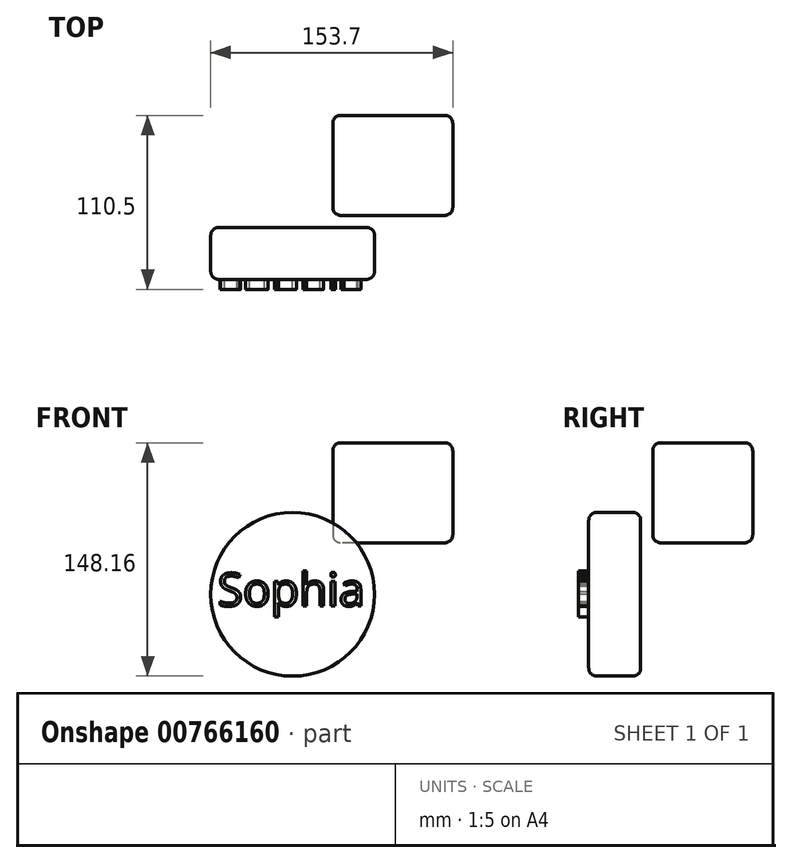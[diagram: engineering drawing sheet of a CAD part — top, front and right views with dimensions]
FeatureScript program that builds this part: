
annotation { "Feature Type Name" : "Feature", "Feature Type Description" : "" }
export const myFeature = defineFeature(function(context is Context, id is Id, definition is map)
    precondition{}
    {
        {
            var Q0;
            Q0=qCreatedBy(makeId("Front.planeOp"),FACE);
            var sketch = newSketch(context, id + "F0", { "sketchPlane" : qUnion([Q0])});
            skCircle(sketch, "E0", {"center": v(-25.5, -28.5) * mm, "radius": 52 * mm});
            skSolve(sketch);
        }
        {
            var Q0;
            Q0 = qSketchRegion(id + "F0", true);
            extrude(context, id + "F1", {"entities" : qUnion([Q0]), "depth" : 33.02 * mm, "offsetDistance" : 25.4 * mm});
        }
        {
            var Q0;
            Q0=makeQuery(id+"F1.opExtrude","SWEPT_FACE",FACE,{"disambiguationData":[OSD([sQuery(id+"F0.wireOp",EDGE,"E0")])]});
            fillet(context, id + "F2", {"entities" : qUnion([Q0]), "radius" : 5.08 * mm, "tangentPropagation" : true, "allowEdgeOverflow" : false});
        }
        {
            var Q0;
            Q0=makeQuery(id+"F1.opExtrude","CAP_FACE",FACE,{"disambiguationData":[OSD([sQuery(id+"F0.wireOp",EDGE,"E0")])],"isStart":false});
            var sketch = newSketch(context, id + "F3", { "sketchPlane" : qUnion([Q0])});
            skText(sketch, "E1", { "text": "Sophia ", "fontName": "OpenSans-Regular.ttf"});
            const initialGuessF3  = {"E1": [-0.07308, -0.03598, 1, 0, 0.02105]};
            skSetInitialGuess(sketch, initialGuessF3);
            skSolve(sketch);
        }
        {
            var Q0;
            Q0 = qSketchRegion(id + "F3", true);
            extrude(context, id + "F4", {"entities" : qUnion([Q0]), "operationType" : NewBodyOperationType.ADD, "depth" : 6.35 * mm, "offsetDistance" : 25.4 * mm});
        }
        {
            var Q0;
            Q0=qCreatedBy(makeId("Right.planeOp"),FACE);
            var sketch = newSketch(context, id + "F5", { "sketchPlane" : qUnion([Q0])});
            skLineSegment(sketch, "E2.bottom", {"start": v(71.13, 67.65) * mm, "end": v(7.63, 67.65) * mm});
            skLineSegment(sketch, "E2.top", {"start": v(71.13, 4.15) * mm, "end": v(7.63, 4.15) * mm});
            skLineSegment(sketch, "E2.left", {"start": v(71.13, 67.65) * mm, "end": v(71.13, 4.15) * mm});
            skLineSegment(sketch, "E2.right", {"start": v(7.63, 67.65) * mm, "end": v(7.63, 4.15) * mm});
            skSolve(sketch);
        }
        {
            var Q0;
            Q0=makeQuery(id+"F5.imprint","IMPRINT",FACE,{"disambiguationData":[TD([[makeQuery(id+"F5.imprint","IMPRINT",EDGE,{"derivedFrom":sQuery(id+"F5.wireOp",EDGE,"E2.bottom")}),1.0]])]});
            extrude(context, id + "F6", {"entities" : qUnion([Q0]), "depth" : 76.2 * mm, "offsetDistance" : 25.4 * mm});
        }
        {
            var Q0;
            Q0=makeQuery(id+"F6.opExtrude","SWEPT_FACE",FACE,{"disambiguationData":[OSD([sQuery(id+"F5.wireOp",EDGE,"E2.bottom")])]});
            var Q1;
            Q1=makeQuery(id+"F6.opExtrude","CAP_EDGE",EDGE,{"disambiguationData":[OSD([sQuery(id+"F5.wireOp",EDGE,"E2.right")])],"isStart":false});
            var Q2;
            Q2=makeQuery(id+"F6.opExtrude","CAP_EDGE",EDGE,{"disambiguationData":[OSD([sQuery(id+"F5.wireOp",EDGE,"E2.right")])],"isStart":true});
            var Q3;
            Q3=makeQuery(id+"F6.opExtrude","SWEPT_EDGE",EDGE,{"disambiguationData":[OSD([sQuery(id+"F5.wireOp",EDGE,"E2.top"),sQuery(id+"F5.wireOp",EDGE,"E2.right")])]});
            var Q4;
            Q4=makeQuery(id+"F6.opExtrude","CAP_EDGE",EDGE,{"disambiguationData":[OSD([sQuery(id+"F5.wireOp",EDGE,"E2.top")])],"isStart":false});
            var Q5;
            Q5=makeQuery(id+"F6.opExtrude","CAP_EDGE",EDGE,{"disambiguationData":[OSD([sQuery(id+"F5.wireOp",EDGE,"E2.left")])],"isStart":false});
            fillet(context, id + "F7", {"entities" : qUnion([Q0, Q1, Q2, Q3, Q4, Q5]), "radius" : 5.08 * mm, "tangentPropagation" : true, "allowEdgeOverflow" : false});
        }
        {
            var Q0;
            Q0=makeQuery(id+"F6.opExtrude","SWEPT_FACE",FACE,{"disambiguationData":[OSD([sQuery(id+"F5.wireOp",EDGE,"E2.left")])]});
            var Q1;
            Q1=makeQuery(id+"F6.opExtrude","SWEPT_EDGE",EDGE,{"disambiguationData":[OSD([sQuery(id+"F5.wireOp",EDGE,"E2.top"),sQuery(id+"F5.wireOp",EDGE,"E2.left")])]});
            var Q2;
            Q2=makeQuery(id+"F6.opExtrude","CAP_EDGE",EDGE,{"disambiguationData":[OSD([sQuery(id+"F5.wireOp",EDGE,"E2.top")])],"isStart":true});
            var Q3;
            Q3=makeQuery(id+"F6.opExtrude","CAP_EDGE",EDGE,{"disambiguationData":[OSD([sQuery(id+"F5.wireOp",EDGE,"E2.left")])],"isStart":true});
            fillet(context, id + "F8", {"entities" : qUnion([Q0, Q1, Q2, Q3]), "radius" : 5.08 * mm, "tangentPropagation" : true, "allowEdgeOverflow" : false});
        }
        {
            var Q0;
            Q0=makeQuery(id+"F6.opExtrude","SWEPT_FACE",FACE,{"disambiguationData":[OSD([sQuery(id+"F5.wireOp",EDGE,"E2.bottom")])]});
            var sketch = newSketch(context, id + "F9", { "sketchPlane" : qUnion([Q0])});
            skCircle(sketch, "E3.cCircle", {"center": v(34.15, 36.6) * mm, "radius": 14.94 * mm, "construction": true});
            skLineSegment(sketch, "E3.0", {"start": v(17.71, 41.84) * mm, "end": v(30.46, 53.46) * mm});
            skLineSegment(sketch, "E3.1", {"start": v(30.46, 53.46) * mm, "end": v(46.9, 48.23) * mm});
            skLineSegment(sketch, "E3.2", {"start": v(46.9, 48.23) * mm, "end": v(50.59, 31.38) * mm});
            skLineSegment(sketch, "E3.3", {"start": v(50.59, 31.38) * mm, "end": v(37.84, 19.76) * mm});
            skLineSegment(sketch, "E3.4", {"start": v(37.84, 19.76) * mm, "end": v(21.4, 24.98) * mm});
            skLineSegment(sketch, "E3.5", {"start": v(21.4, 24.98) * mm, "end": v(17.71, 41.84) * mm});
            skPoint(sketch, "E3.0.midPoint", {"position": v(24.08, 47.65) * mm});
            skSolve(sketch);
        }
        {
            var Q0;
            Q0=makeQuery(id+"F9.imprint","IMPRINT",FACE,{"disambiguationData":[TD([[makeQuery(id+"F9.imprint","IMPRINT",EDGE,{"derivedFrom":sQuery(id+"F9.wireOp",EDGE,"E3.0")}),-1.0]])]});
            extrude(context, id + "F10", {"entities" : qUnion([Q0]), "operationType" : NewBodyOperationType.ADD, "oppositeDirection" : true, "depth" : 25.4 * mm, "offsetDistance" : 25.4 * mm});
        }
    });
